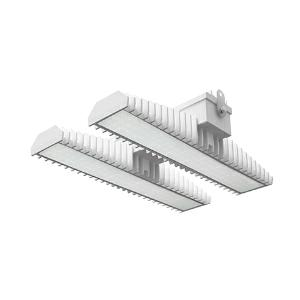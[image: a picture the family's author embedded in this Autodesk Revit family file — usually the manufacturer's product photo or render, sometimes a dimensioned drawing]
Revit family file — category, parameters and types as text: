
# Revit family: 3f_filippi_-_3f_lem_concentrato_3f_filippi_-_59164_a0812_-_3f_lem_2_led_100-865_cr_conc___vs_607d
name_source: partatom
category: Lighting Fixtures
units: mm (PartAtom-declared; Revit-internal decimal feet)

## family parameters
Cut with Voids When Loaded = No
Host = Face
Light Source = No
Part Type = Normal
Room Calculation Point = No
Round Connector Dimension = Use Diameter
Shared = No

## types (1)
- 3F Filippi - 3F LEM Concentrato (1 x LED, 13214 lm, 109 W, 6500 K)
    Apparent Load = 109 VA
    Approval mark = CE
    CIE Flux Codes = 78 93 98 100 100
    Color Rendering = 80
    Color Temperature = 6500 K
    Control Gear = Electronic ballast
    Default Elevation = 1800 mm
    Description = Industrial luminaire with high light output and high luminous efficiency designed with the most innovative technologies for environments with temperature up to 55°C.

ILLUMINOTECHNICAL
Luminous efficiency 100% (DLOR 98%, ULOR 2%).
Initial luminous flux of the luminaire 13214 lm.
Direct symmetric narrow distribution: the illuminated area has a elliptical shape.
Installation Interdistance Transv.D = 0.60 x hu - Long.D = 0.91 x hu.
Tabular UGR (CIE 117 - 4H-8H; S=0.25H; 70/50/20): RUG 19.5 - 21.
Beam angle: 38° - 61°.
Luminous efficacy 121 lm/W.
Lifetime (L93/B10): 30000 h. (tq+25°C)
Lifetime (L90/B10): 50000 h. (tq+25°C)
Lifetime (L85/B10): 80000 h. (tq+25°C)
Lifetime (L80/B10): 100000 h. (tq+25°C)
Lifetime (L85/B10): 50000 h. (tq+55°C)
Sudden decreased luminous flux after 50000 hours: 0% (C0).
Photobiological safety in compliance with IEC/TR 62778: RG0 risk exempt, (IEC 62471).
In compliance with IEC/EN 62722-2-1 - IEC/EN 62717 standards.

SOURCE
2 Mid-Power linear LED modules 50W/865.
Energy efficiency class (UE 2019/2020 - UE 2019/2015): C.
CIE 13.3 Colour rendering index: CRI >80 (R9 <50%).
IES TM-30 Fidelity Index: Rf = 84 Rg = 95.
CCT nominal colour temperature 6500 K.
Colour initial tolerance (MacAdam): SDCM 3.

MECHANICAL
Passive modular heatsinks in die-casted aluminium, painted in white colour.
To optimize the thermal management of the LED module, the heatsinks are oversized and provided with self-cleaning of cooling fins.
Wiring body in aluminium and galvanised steel anchored solidly to the sinks and thermally separated.
3F Lens lenses with high luminous efficiency, transparent methacrylate (PMMA), fixed to the LED modules.
Fixing brackets in stainless steel.
Luminaire with limited surface temperature. - D - (EN 60598-2-24)
Dimensions: 470x542 mm, height 133 mm. Weight 10.52 kg.
IP65 protection degree.
Mechanical strength to impacts IK06 (1 joule).
Glow-wire test resistance 650°C.

ELECTRICAL
Halogen Free electronic wiring 230V-50/60Hz, power factor 0.97, THD <25%, constant output current, class I, 1 driver.
Power of the luminaire 109 W.
ENEC - CE.
SAFE FLICKER: PstLM=<1 and SVM=<0.4 (IEC TR 61547-1 and IEC TR 63158), to ensure a more comfortable and safe light.
Luminaire compliant with EN 60598-2-22 for power supply from a centralised emergency system CPSS (Central Power Supply System), not incorporated in the luminaire - high risk areas excluded. The default power and flux are 100% in AC and 100% in DC.
Ambient temperature from -30°C to +55°C.
Temperature class T6 max 85°C.
Quick connection via M20 3P connector with 9-13 mm tightening range.
Power unit positioned on a separate compartment by the LED module to ensure optimum temperatures of cabling components, to be inspectable and maintainable.
Relative humidity UR: <85%.

INSTALLATION
Ceiling / Suspended / Wall.
All accessories dedicated to this product are available on the Catalog and on our website www.3F-Filippi.com.

ACCESSORIES
A0812 - Anti-glare microprismatic VS moulded glass, tempered, not flammable, with sealing gasket.
One required for each light module. The pack contains 10 pieces.

APPLICATIONS
In commercial environments, exhibition and industrial areas, stores, open areas.
Applications with high ambient temperature up to 55°C.
Environments in which it is necessary a total protection against falling fragments (eg environments with foodstuffs or machines with moving parts or with extreme temperature changes), use luminaires with polycarbonate lenses.

WARNING
Fixture not suitable for cold stores with an ambient temperature <0°C and/or relative humidity >85%.
Luminaire designed for disposal/recycling at end-of-life.
Replaceable (LED only) light source by a professional. Replaceable control gear by a professional.
    Height = 133 mm  [stored 0.436352 ft]
    Lamp = 1 x LED
    Lamp Light Flux = 13214 lm
    Lamp Power = 109 W
    Lamp count = 1
    Length = 470 mm
    Lifetime = 50000 h
    Luminous efficacy = 121 lm/W
    Manufacturer = 3F Filippi
    ModVariant = No
    Model = 3F Filippi - 59164+A0812 - 3F LEM 2 LED 100-865 CR CONC + VS
    Mounting Place = Ceiling
    Mounting Type = Pendant
    Number of Poles = 1
    OnlyDefault = Yes
    Power Factor = 1
    Product Name = 3F Filippi - 3F LEM Concentrato
    Product group = pendant luminaire
    ProductGroupID = 9
    Protection Class = Protection class I
    Protection Degree = IP 65
    RLX_Detail_Level = 1
    RLX_Emergency_Light_Flux = 0 lm
    RLX_Emergency_Type = 0
    RLX_Emergency_Type_DB = No
    RlxData = <blob elided: 95921 chars, md5=587ff075>
    Socket = socket
    Standby Power = 0 W
    System Light Flux = 13214 lm
    System Power = 109 W
    Type Comments = Product without accessories
    Type Image = 3f_filippi_-_lem_2__a0812.jpg
    URL = http://relux.com
    VarID = ---
    Voltage = 0 V
    Weight = 0.00 kg
    Width = 542 mm

note: [stored X ft] marks values corroborated as IEEE doubles in the binary element streams (Revit-internal decimal feet)

## geometry (parser evidence)
native form markers: Blend x4, Sweep x13
no freeform markers — native parametric forms only
